# Revit family: HD K 110 215 WIL
name_source: partatom
category: Generic Models
revit_build: Autodesk Revit LT 2014 (Build: 20130308_1515(x64)
units: mm (PartAtom-declared; Revit-internal decimal feet)

## types (1)
- Max lintel length 4050mm
    CPD Information = Available for Keystone Lintels Ltd from ribacpd.com
    Corrosion = Keystone’s standard range of lintels are manufactured from high quality grade pre-galvanized carbon steel with a zinc coating of 600
    End Bearing = 150 mm
    Fire Performance = Keystone lintels have been subjected to a fire test (WARRES No. 101263) in accordance with BS 476-20: 1987, at Exova Warrington Fire and achieved a one hour fire performance.
    Keynote = F30/755
    Manufacturer = Keystone
    Material - Galvanised Steel = To BS EN 10346: 2009. DX51D plus Z600 or grade Z275 to BS 5977-2: 1983 (BS EN 845-2: 2003).
    Material - Stainless Steel = Grade 304 2b 1.4307 to BS EN 10088-2. Other grades available on request: contact manufacturer.
    Max Clear Span = 4050 mm  [stored 13.2874 ft]
    Max Length = 4050 mm  [stored 13.2874 ft]
    Min Clear Span = 300 mm
    Min Length = 600 mm  [stored 1.9685 ft]
    Model = HD/K 110 215 WIL
    RIBA Productor Selector = available for Keystone Lintels Ltd from Keystone Lintels Ltd from ribaproductselector.com
    Structural Performance = The Keystone lintel range has safe working loads as detailed in each applicable loading table in the Keystone Lintel Guide brochure. The structural performance figures within each table have been ascertained by testing in accordance with the requirements of standards BS EN 5977-2: 1983 and BS EN 845-2: 2003.
    URL = http://www.keystonelintels.co.uk

note: [stored X ft] marks values corroborated as IEEE doubles in the binary element streams (Revit-internal decimal feet)

## geometry (parser evidence)
native form markers: Sweep x1
no freeform markers — native parametric forms only
